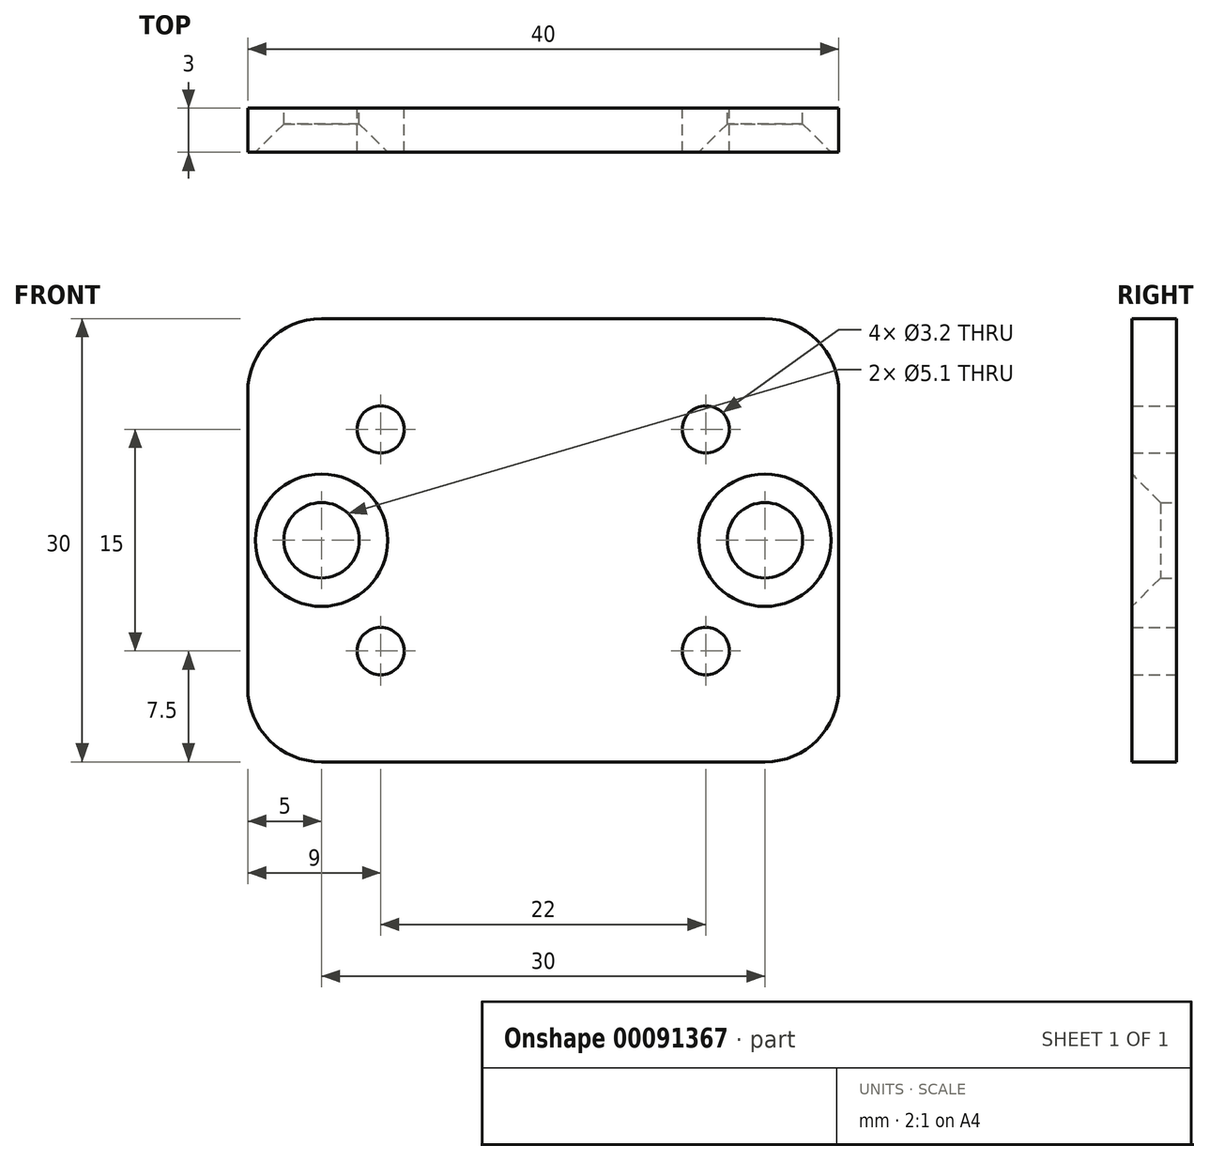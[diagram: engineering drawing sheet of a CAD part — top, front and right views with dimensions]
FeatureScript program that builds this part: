
annotation { "Feature Type Name" : "Feature", "Feature Type Description" : "" }
export const myFeature = defineFeature(function(context is Context, id is Id, definition is map)
    precondition{}
    {
        {
            var Q0;
            Q0=qCreatedBy(makeId("Front.planeOp"),FACE);
            var sketch = newSketch(context, id + "F0", { "sketchPlane" : qUnion([Q0])});
            skLineSegment(sketch, "E0", {"start": v(0, 19.24) * mm, "end": v(0, -19.3) * mm, "construction": true});
            skLineSegment(sketch, "E1", {"start": v(-30.55, 0) * mm, "end": v(30.12, 0) * mm, "construction": true});
            skLineSegment(sketch, "E2", {"start": v(-20, 15) * mm, "end": v(-20, -15) * mm});
            skLineSegment(sketch, "E3", {"start": v(-20, -15) * mm, "end": v(20, -15) * mm});
            skLineSegment(sketch, "E4", {"start": v(20, -15) * mm, "end": v(20, 15) * mm});
            skLineSegment(sketch, "E5", {"start": v(20, 15) * mm, "end": v(-20, 15) * mm});
            skPoint(sketch, "E6", {"position": v(-20, 0) * mm});
            skSolve(sketch);
        }
        {
            var Q0;
            Q0=makeQuery(id+"F0.imprint","IMPRINT",FACE,{"disambiguationData":[TD([[makeQuery(id+"F0.imprint","IMPRINT",EDGE,{"derivedFrom":sQuery(id+"F0.wireOp",EDGE,"E2")}),1.0]])]});
            extrude(context, id + "F1", {"entities" : qUnion([Q0]), "oppositeDirection" : true, "depth" : 3 * mm});
        }
        {
            var Q0;
            Q0=makeQuery(id+"F1.opExtrude","CAP_FACE",FACE,{"disambiguationData":[OSD([sQuery(id+"F0.wireOp",EDGE,"E2"),sQuery(id+"F0.wireOp",EDGE,"E3"),sQuery(id+"F0.wireOp",EDGE,"E4"),sQuery(id+"F0.wireOp",EDGE,"E5")])],"isStart":true});
            var sketch = newSketch(context, id + "F2", { "sketchPlane" : qUnion([Q0])});
            skLineSegment(sketch, "E7", {"start": v(20, 0) * mm, "end": v(-20, 0) * mm, "construction": true});
            skLineSegment(sketch, "E8", {"start": v(0, 15) * mm, "end": v(0, -15) * mm, "construction": true});
            skPoint(sketch, "E9", {"position": v(11, 7.5) * mm});
            skPoint(sketch, "E10", {"position": v(-11, 7.5) * mm});
            skPoint(sketch, "E11", {"position": v(-11, -7.5) * mm});
            skPoint(sketch, "E12", {"position": v(11, -7.5) * mm});
            skPoint(sketch, "E13", {"position": v(-15, 0) * mm});
            skPoint(sketch, "E14", {"position": v(15, 0) * mm});
            skSolve(sketch);
        }
        {
            var Q0;
            Q0=sQuery(id+"F2.wireOp",VERTEX,"E10");
            var Q1;
            Q1=sQuery(id+"F2.wireOp",VERTEX,"E11");
            var Q2;
            Q2=sQuery(id+"F2.wireOp",VERTEX,"E9");
            var Q3;
            Q3=sQuery(id+"F2.wireOp",VERTEX,"E12");
            var Q4;
            Q4=makeQuery(id+"F1.opExtrude","SWEPT_BODY",BODY,{"disambiguationData":[OSD([sQuery(id+"F0.wireOp",EDGE,"E2"),sQuery(id+"F0.wireOp",EDGE,"E3"),sQuery(id+"F0.wireOp",EDGE,"E4"),sQuery(id+"F0.wireOp",EDGE,"E5")])]});
            hole(context, id + "F3", {"style" : HoleStyle.SIMPLE, "endStyle" : HoleEndStyle.THROUGH, "standardTappedOrClearance" : lookupTablePath({ "standard" : "ISO", "engagement" : "75%", "pitch" : "0.75 mm", "size" : "M4", "type" : "Tapped" }), "standardBlindInLast" : lookupTablePath({ "standard" : "ISO", "engagement" : "75%", "pitch" : "0.75 mm", "size" : "M4", "type" : "Tapped" }), "holeDiameter" : 3.2 * mm, "locations" : qUnion([Q0, Q1, Q2, Q3]), "scope" : qUnion([Q4]), "isTappedThrough" : true, "showTappedDepth" : true, "startStyle" : HoleStartStyle.SKETCH});
        }
        {
            var Q0;
            Q0=sQuery(id+"F2.wireOp",VERTEX,"E13");
            var Q1;
            Q1=sQuery(id+"F2.wireOp",VERTEX,"E14");
            var Q2;
            Q2=makeQuery(id+"F1.opExtrude","SWEPT_BODY",BODY,{"disambiguationData":[OSD([sQuery(id+"F0.wireOp",EDGE,"E2"),sQuery(id+"F0.wireOp",EDGE,"E3"),sQuery(id+"F0.wireOp",EDGE,"E4"),sQuery(id+"F0.wireOp",EDGE,"E5")])]});
            hole(context, id + "F4", {"style" : HoleStyle.C_SINK, "endStyle" : HoleEndStyle.THROUGH, "standardTappedOrClearance" : lookupTablePath({ "standard" : "ISO", "size" : "5.1", "type" : "Drilled" }), "standardBlindInLast" : lookupTablePath({ "standard" : "ISO", "size" : "5.1", "type" : "Drilled" }), "holeDiameter" : 5.1 * mm, "cSinkDiameter" : 8.96 * mm, "cSinkAngle" : 90 * degree, "locations" : qUnion([Q0, Q1]), "scope" : qUnion([Q2]), "isTappedThrough" : true, "startStyle" : HoleStartStyle.SKETCH});
        }
        {
            var Q0;
            Q0=makeQuery(id+"F1.opExtrude","SWEPT_EDGE",EDGE,{"disambiguationData":[OSD([sQuery(id+"F0.wireOp",EDGE,"E4"),sQuery(id+"F0.wireOp",EDGE,"E5")])]});
            var Q1;
            Q1=makeQuery(id+"F1.opExtrude","SWEPT_EDGE",EDGE,{"disambiguationData":[OSD([sQuery(id+"F0.wireOp",EDGE,"E3"),sQuery(id+"F0.wireOp",EDGE,"E4")])]});
            var Q2;
            Q2=makeQuery(id+"F1.opExtrude","SWEPT_EDGE",EDGE,{"disambiguationData":[OSD([sQuery(id+"F0.wireOp",EDGE,"E2"),sQuery(id+"F0.wireOp",EDGE,"E3")])]});
            var Q3;
            Q3=makeQuery(id+"F1.opExtrude","SWEPT_EDGE",EDGE,{"disambiguationData":[OSD([sQuery(id+"F0.wireOp",EDGE,"E2"),sQuery(id+"F0.wireOp",EDGE,"E5")])]});
            fillet(context, id + "F5", {"entities" : qUnion([Q0, Q1, Q2, Q3]), "radius" : 5 * mm, "tangentPropagation" : true, "allowEdgeOverflow" : false});
        }
    });
